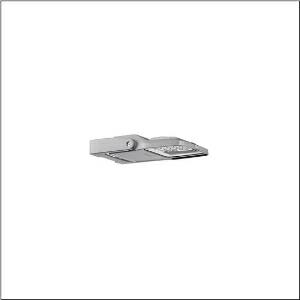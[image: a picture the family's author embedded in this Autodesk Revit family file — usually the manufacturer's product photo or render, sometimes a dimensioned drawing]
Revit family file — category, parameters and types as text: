
# Revit family: floodlight_fl_21_micro___pl52_5xa7762a2d2a_b309
name_source: partatom
category: Lighting Fixtures
units: mm (PartAtom-declared; Revit-internal decimal feet)

## family parameters
Cut with Voids When Loaded = No
Host = Face
Light Source = No
Part Type = Normal
Room Calculation Point = No
Round Connector Dimension = Use Diameter
Shared = No

## types (1)
- --- (1 x LED, 2890 lm, 23.1 W, 3000K)
    Apparent Load = 23 VA
    CIE Flux Codes = 26 60 98 100 100
    Color Rendering = 70
    Color Temperature = 3000K
    Default Elevation = 1800 mm
    Description = Floodlight FL 21 micro, floodlight, primary light control with lens, of PMMA, primary optical cover: protective disc, of toughened safety glass, transparent, light distribution: PL52, light emission: direct distribution, installation type: surface-mounted, LED, High Power LED, rated luminous flux: 2.890lm, luminous efficacy: 125lm/W, light colour: 730, colour temperature: 3000K, control gear: ECG iQ, control: Auto-Match, Temp-Guard, Night-Set, Smart-Wire, Desk-Remote (wireless, voltage-free reading and setting of iQ features in the workshop via application-optimized NFC function/RFID function), optimised constant luminous flux control (CLO 2.0), Street-Remote, with terminal, 6-pole, mains connection: 220..240V, AC, 50/60Hz, start of lifetime: 23W, end of lifetime: 24W, reduction: 11W, luminaire housing, of diecast aluminium, powder-coated, Siteco® metallic grey (DB 702S), corrosivity category C5 according to DIN EN ISO 12944, design bracket, of diecast aluminium, powder-coated, Siteco® metallic grey (DB 702S), protection rating (complete): IP66, insulation class (complete): insulation class II (safety insulation), certification: CE, protection symbol: D, impact resistance: IK07, permissible operating ambient temperature: -40..+40°C, permissible operating ambient temperature for outdoor applications: -40..+50°C, standard: DIN EN 12944, packaging unit: 1 piece

Light Distribution: PL52
    Height = 65 mm
    Lamp = 1 x LED
    Lamp Light Flux = 2890 lm
    Lamp Power = 23.1 W
    Lamp count = 1
    Length = 312 mm
    Luminous efficacy = 125 lm/W
    Manufacturer = Siteco
    ModVariant = No
    Model = 5XA7762A2D2A
    Number of Poles = 1
    OnlyDefault = Yes
    Power Factor = 1
    Product Name = Floodlight FL 21 micro | PL52
    Product group = floodlight | pylon top
    ProductGroupID = 6101
    Protection Class = Protection class II
    Protection Degree = IP 66
    RLX_Detail_Level = 1
    RlxData = <blob elided: 97565 chars, md5=1b297293>
    Socket = socket
    Standby Power = 0 W
    System Light Flux = 2890 lm
    System Power = 23 W
    Type Comments = factory setting: luminous flux: 100 % | dim-lin: 254 | 455 mA
    Type Image = l_1006878.jpg
    URL = http://relux.com
    VarID = @adj_090577
    Voltage = 0 V
    Weight = 0.00 kg
    Width = 230 mm

## geometry (parser evidence)
native form markers: Blend x4, Sweep x15
no freeform markers — native parametric forms only
